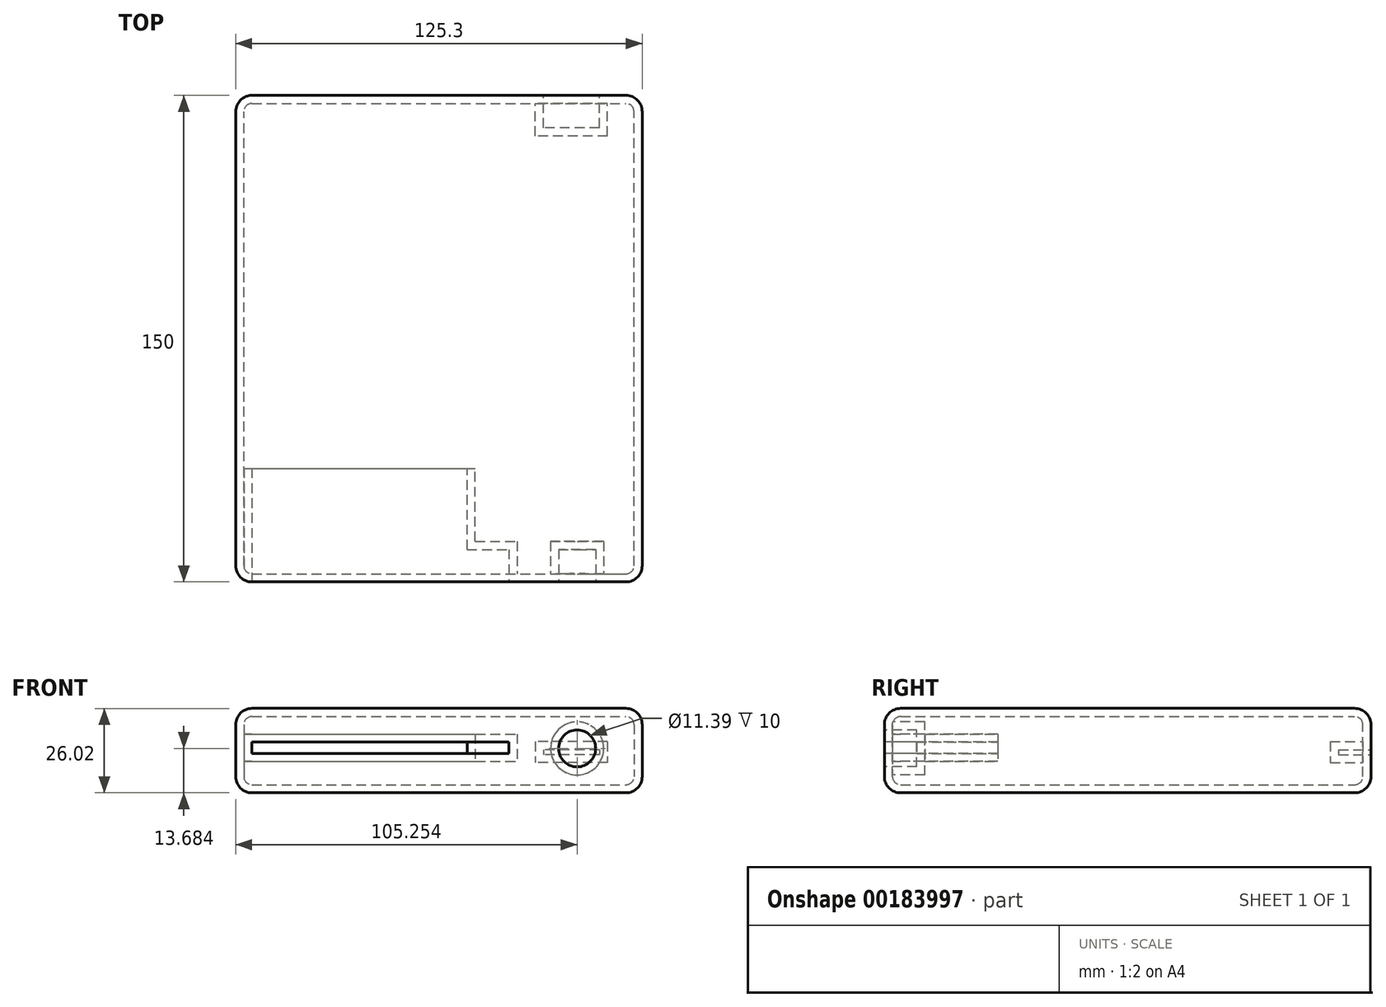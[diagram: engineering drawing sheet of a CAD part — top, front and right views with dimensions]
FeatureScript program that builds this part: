
annotation { "Feature Type Name" : "Feature", "Feature Type Description" : "" }
export const myFeature = defineFeature(function(context is Context, id is Id, definition is map)
    precondition{}
    {
        {
            var Q0;
            Q0=qCreatedBy(makeId("Front.planeOp"),FACE);
            var sketch = newSketch(context, id + "F0", { "sketchPlane" : qUnion([Q0])});
            skLineSegment(sketch, "E0.bottom", {"start": v(-59.18, 19.18) * mm, "end": v(66.12, 19.18) * mm});
            skLineSegment(sketch, "E0.top", {"start": v(-59.18, -6.84) * mm, "end": v(66.12, -6.84) * mm});
            skLineSegment(sketch, "E0.left", {"start": v(-59.18, 19.18) * mm, "end": v(-59.18, -6.84) * mm});
            skLineSegment(sketch, "E0.right", {"start": v(66.12, 19.18) * mm, "end": v(66.12, -6.84) * mm});
            skSolve(sketch);
        }
        {
            var Q0;
            Q0 = qSketchRegion(id + "F0", true);
            extrude(context, id + "F1", {"entities" : qUnion([Q0]), "depth" : 150 * mm});
        }
        {
            var Q0;
            Q0=makeQuery(id+"F1.opExtrude","CAP_FACE",FACE,{"disambiguationData":[OSD([sQuery(id+"F0.wireOp",EDGE,"E0.bottom"),sQuery(id+"F0.wireOp",EDGE,"E0.top"),sQuery(id+"F0.wireOp",EDGE,"E0.left"),sQuery(id+"F0.wireOp",EDGE,"E0.right")])],"isStart":false});
            var Q1;
            Q1=makeQuery(id+"F1.opExtrude","CAP_EDGE",EDGE,{"disambiguationData":[OSD([sQuery(id+"F0.wireOp",EDGE,"E0.bottom")])],"isStart":false});
            var Q2;
            Q2=makeQuery(id+"F1.opExtrude","SWEPT_FACE",FACE,{"disambiguationData":[OSD([sQuery(id+"F0.wireOp",EDGE,"E0.left")])]});
            var Q3;
            Q3=makeQuery(id+"F1.opExtrude","SWEPT_FACE",FACE,{"disambiguationData":[OSD([sQuery(id+"F0.wireOp",EDGE,"E0.right")])]});
            var Q4;
            Q4=makeQuery(id+"F1.opExtrude","CAP_FACE",FACE,{"disambiguationData":[OSD([sQuery(id+"F0.wireOp",EDGE,"E0.bottom"),sQuery(id+"F0.wireOp",EDGE,"E0.top"),sQuery(id+"F0.wireOp",EDGE,"E0.left"),sQuery(id+"F0.wireOp",EDGE,"E0.right")])],"isStart":true});
            fillet(context, id + "F2", {"entities" : qUnion([Q0, Q1, Q2, Q3, Q4]), "radius" : 5 * mm, "tangentPropagation" : true, "allowEdgeOverflow" : false});
        }
        {
            var Q0;
            Q0=makeQuery(id+"F1.opExtrude","CAP_FACE",FACE,{"disambiguationData":[OSD([sQuery(id+"F0.wireOp",EDGE,"E0.bottom"),sQuery(id+"F0.wireOp",EDGE,"E0.top"),sQuery(id+"F0.wireOp",EDGE,"E0.left"),sQuery(id+"F0.wireOp",EDGE,"E0.right")])],"isStart":false});
            var sketch = newSketch(context, id + "F3", { "sketchPlane" : qUnion([Q0])});
            skLineSegment(sketch, "E1.bottom", {"start": v(-54.18, 8.77) * mm, "end": v(25.06, 8.77) * mm});
            skLineSegment(sketch, "E1.top", {"start": v(-54.18, 5.3) * mm, "end": v(25.06, 5.3) * mm});
            skLineSegment(sketch, "E1.left", {"start": v(-54.18, 8.77) * mm, "end": v(-54.18, 5.3) * mm});
            skLineSegment(sketch, "E1.right", {"start": v(25.06, 8.77) * mm, "end": v(25.06, 5.3) * mm});
            skSolve(sketch);
        }
        {
            var Q0;
            Q0=makeQuery(id+"F3.imprint","IMPRINT",FACE,{"disambiguationData":[TD([[makeQuery(id+"F3.imprint","IMPRINT",EDGE,{"derivedFrom":sQuery(id+"F3.wireOp",EDGE,"E1.bottom")}),-1.0]])]});
            extrude(context, id + "F4", {"entities" : qUnion([Q0]), "operationType" : NewBodyOperationType.REMOVE, "oppositeDirection" : true, "depth" : 35 * mm});
        }
        {
            var Q0;
            Q0=makeQuery(id+"F1.opExtrude","CAP_FACE",FACE,{"disambiguationData":[OSD([sQuery(id+"F0.wireOp",EDGE,"E0.bottom"),sQuery(id+"F0.wireOp",EDGE,"E0.top"),sQuery(id+"F0.wireOp",EDGE,"E0.left"),sQuery(id+"F0.wireOp",EDGE,"E0.right")])],"isStart":false});
            var sketch = newSketch(context, id + "F5", { "sketchPlane" : qUnion([Q0])});
            skCircle(sketch, "E2", {"center": v(46.07, 6.84) * mm, "radius": 5.7 * mm});
            skSolve(sketch);
        }
        {
            var Q0;
            Q0=makeQuery(id+"F5.imprint","IMPRINT",FACE,{"disambiguationData":[TD([[makeQuery(id+"F5.imprint","IMPRINT",EDGE,{"derivedFrom":sQuery(id+"F5.wireOp",EDGE,"E2")}),1.0]])]});
            extrude(context, id + "F6", {"entities" : qUnion([Q0]), "operationType" : NewBodyOperationType.ADD, "depth" : 25 * mm});
        }
        {
            var Q0;
            Q0=makeQuery(id+"F6.opExtrude","CAP_FACE",FACE,{"disambiguationData":[OSD([sQuery(id+"F5.wireOp",EDGE,"E2")])],"isStart":false});
            extrude(context, id + "F7", {"entities" : qUnion([Q0]), "operationType" : NewBodyOperationType.REMOVE, "oppositeDirection" : true, "depth" : 35 * mm});
        }
        {
            var Q0;
            Q0=makeQuery(id+"F4.boolean.opBoolean","COPY",FACE,{"derivedFrom":makeQuery(id+"F4.opExtrude","CAP_FACE",FACE,{"disambiguationData":[OSD([sQuery(id+"F3.wireOp",EDGE,"E1.bottom"),sQuery(id+"F3.wireOp",EDGE,"E1.top"),sQuery(id+"F3.wireOp",EDGE,"E1.left"),sQuery(id+"F3.wireOp",EDGE,"E1.right")])],"isStart":false})});
            var sketch = newSketch(context, id + "F8", { "sketchPlane" : qUnion([Q0])});
            skLineSegment(sketch, "E3.bottom", {"start": v(12.17, 8.77) * mm, "end": v(25.06, 8.77) * mm});
            skLineSegment(sketch, "E3.top", {"start": v(12.17, 5.3) * mm, "end": v(25.06, 5.3) * mm});
            skLineSegment(sketch, "E3.left", {"start": v(12.17, 8.77) * mm, "end": v(12.17, 5.3) * mm});
            skLineSegment(sketch, "E3.right", {"start": v(25.06, 8.77) * mm, "end": v(25.06, 5.3) * mm});
            skSolve(sketch);
        }
        {
            var Q0;
            Q0=makeQuery(id+"F8.imprint","IMPRINT",FACE,{"disambiguationData":[TD([[makeQuery(id+"F8.imprint","IMPRINT",EDGE,{"derivedFrom":sQuery(id+"F8.wireOp",EDGE,"E3.bottom")}),-1.0]])]});
            extrude(context, id + "F9", {"entities" : qUnion([Q0]), "operationType" : NewBodyOperationType.ADD, "depth" : 25 * mm});
        }
        {
            var Q0;
            Q0=makeQuery(id+"F1.opExtrude","CAP_FACE",FACE,{"disambiguationData":[OSD([sQuery(id+"F0.wireOp",EDGE,"E0.bottom"),sQuery(id+"F0.wireOp",EDGE,"E0.top"),sQuery(id+"F0.wireOp",EDGE,"E0.left"),sQuery(id+"F0.wireOp",EDGE,"E0.right")])],"isStart":true});
            var sketch = newSketch(context, id + "F10", { "sketchPlane" : qUnion([Q0])});
            skLineSegment(sketch, "E4.bottom", {"start": v(-52.94, 6.45) * mm, "end": v(-35.66, 6.45) * mm});
            skLineSegment(sketch, "E4.top", {"start": v(-52.94, 4.92) * mm, "end": v(-35.66, 4.92) * mm});
            skLineSegment(sketch, "E4.left", {"start": v(-52.94, 6.45) * mm, "end": v(-52.94, 4.92) * mm});
            skLineSegment(sketch, "E4.right", {"start": v(-35.66, 6.45) * mm, "end": v(-35.66, 4.92) * mm});
            skSolve(sketch);
        }
        {
            var Q0;
            Q0 = qSketchRegion(id + "F10", true);
            extrude(context, id + "F11", {"entities" : qUnion([Q0]), "operationType" : NewBodyOperationType.ADD, "depth" : 25 * mm});
        }
        {
            var Q0;
            Q0=makeQuery(id+"F11.opExtrude","CAP_FACE",FACE,{"disambiguationData":[OSD([sQuery(id+"F10.wireOp",EDGE,"E4.bottom"),sQuery(id+"F10.wireOp",EDGE,"E4.top"),sQuery(id+"F10.wireOp",EDGE,"E4.left"),sQuery(id+"F10.wireOp",EDGE,"E4.right")])],"isStart":false});
            extrude(context, id + "F12", {"entities" : qUnion([Q0]), "operationType" : NewBodyOperationType.REMOVE, "oppositeDirection" : true, "depth" : 35 * mm});
        }
        {
            var Q0;
            Q0=makeQuery(id+"F4.boolean.opBoolean","COPY",FACE,{"derivedFrom":makeQuery(id+"F4.opExtrude","CAP_FACE",FACE,{"disambiguationData":[OSD([sQuery(id+"F3.wireOp",EDGE,"E1.bottom"),sQuery(id+"F3.wireOp",EDGE,"E1.top"),sQuery(id+"F3.wireOp",EDGE,"E1.left"),sQuery(id+"F3.wireOp",EDGE,"E1.right")])],"isStart":false})});
            shell(context, id + "F13", {"entities" : qUnion([Q0]), "thickness" : 2.5 * mm});
        }
    });
